# Revit family: NXPS_Series
name_source: partatom
category: Electrical Equipment
units: mm (PartAtom-declared; Revit-internal decimal feet)

## family parameters
Cut with Voids When Loaded = No
Host = Face
OmniClass Number = 23.80.30.11.17
OmniClass Title = Distribution Boards and Control Panels
Part Type = Equipment Switch
Room Calculation Point = No
Round Connector Dimension = Use Diameter
Shared = No

## types (4) — shared parameters
Apparent Load = 0.000 VA
Certifications = UL916, UL924 and cUL
Connector Description 1 = Power Supply
Default Elevation = 48 "
Description = Lighting Control Panels and Relays
Device Material = Gray
Frequency = 60 Hz
Load Classification = Power
Manufacturer = NX Lighting Controls
Model = NXPS Series
Network Interface = Ethernet 10 base-T via  network cable, integral 2-port Ethernet hub
Operating Environment = Interior, Dry location
Operating Temperature = 0° to 50°C (32° to 112°F)
Power Factor = 1
Programming and Configuration = Programmable via web browser user interface, requires NXAC Area Controller
Relative Humidity = 10 to 95%
Type Comments = Electrical Equipment
URL = https://www.currentlighting.com
Voltage = 120V
Warranty = Five-year limited
zz Length 2 = 20 "
zz Length 3 = 4.08 "

## per-type parameters (varying)
| type | Assembly Code | zz Length 1 |
| NXP32 | D50 | 30.5 " |
| NXP8 | D50 | 18.25 " |
| NXP24 | D50 | 24 " |
| NXP48 | D5030 | 43.5 " |

## geometry (parser evidence)
native form markers: Sweep x3
no freeform markers — native parametric forms only
